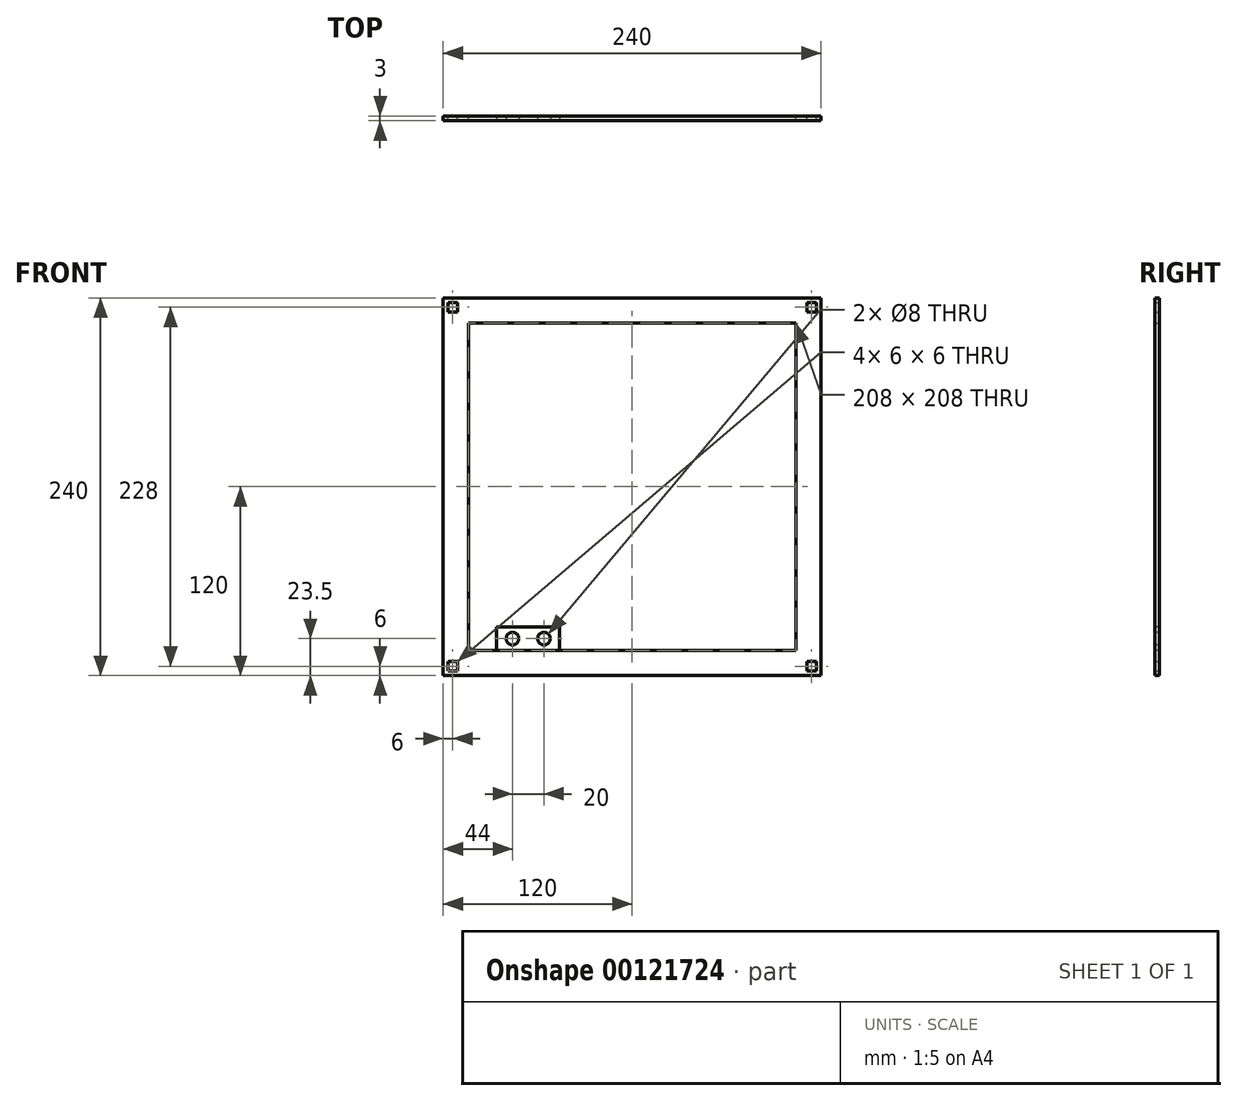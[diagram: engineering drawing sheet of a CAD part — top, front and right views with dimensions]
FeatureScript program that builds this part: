
annotation { "Feature Type Name" : "Feature", "Feature Type Description" : "" }
export const myFeature = defineFeature(function(context is Context, id is Id, definition is map)
    precondition{}
    {
        {
            assignVariable(context, id + "F0", {"name" : "thicknessWood", "anyValue" : 3});
        }
        {
            var Q0;
            Q0=qCreatedBy(makeId("Front.planeOp"),FACE);
            var sketch = newSketch(context, id + "F1", { "sketchPlane" : qUnion([Q0])});
            skLineSegment(sketch, "E0.bottom", {"start": v(0, 0) * mm, "end": v(240, 0) * mm});
            skLineSegment(sketch, "E0.top", {"start": v(0, 240) * mm, "end": v(240, 240) * mm});
            skLineSegment(sketch, "E0.left", {"start": v(0, 0) * mm, "end": v(0, 240) * mm});
            skLineSegment(sketch, "E0.right", {"start": v(240, 0) * mm, "end": v(240, 240) * mm});
            skLineSegment(sketch, "E1.bottom", {"start": v(16, 224) * mm, "end": v(224, 224) * mm});
            skLineSegment(sketch, "E1.top", {"start": v(16, 16) * mm, "end": v(224, 16) * mm});
            skLineSegment(sketch, "E1.left", {"start": v(16, 224) * mm, "end": v(16, 16) * mm});
            skLineSegment(sketch, "E1.right", {"start": v(224, 224) * mm, "end": v(224, 16) * mm});
            skLineSegment(sketch, "E2.bottom", {"start": v(9, 237) * mm, "end": v(3, 237) * mm});
            skLineSegment(sketch, "E2.top", {"start": v(9, 231) * mm, "end": v(3, 231) * mm});
            skLineSegment(sketch, "E2.left", {"start": v(9, 237) * mm, "end": v(9, 231) * mm});
            skLineSegment(sketch, "E2.right", {"start": v(3, 237) * mm, "end": v(3, 231) * mm});
            skLineSegment(sketch, "E3", {"start": v(120, 240) * mm, "end": v(120, 0) * mm, "construction": true});
            skLineSegment(sketch, "E4", {"start": v(0, 120) * mm, "end": v(240, 120) * mm, "construction": true});
            skSolve(sketch);
        }
        {
            var Q0;
            Q0=makeQuery(id+"F1.imprint","IMPRINT",FACE,{"disambiguationData":[TD([[makeQuery(id+"F1.imprint","IMPRINT",EDGE,{"derivedFrom":sQuery(id+"F1.wireOp",EDGE,"E0.bottom")}),1.0]])]});
            var Q1;
            Q1=makeQuery(id+"F1.imprint","IMPRINT",FACE,{"disambiguationData":[TD([[makeQuery(id+"F1.imprint","IMPRINT",EDGE,{"derivedFrom":sQuery(id+"F1.wireOp",EDGE,"E2.bottom")}),1.0]])]});
            var Q2;
            Q2=sQuery(id+"F1.wireOp",EDGE,"E1.left");
            extrude(context, id + "F2", {"entities" : qUnion([Q0, Q1]), "surfaceEntities" : qUnion([Q2]), "depth" : (getVariable(context, 'thicknessWood')) * mm});
        }
        {
            var Q0;
            Q0=makeQuery(id+"F1.imprint","IMPRINT",FACE,{"disambiguationData":[TD([[makeQuery(id+"F1.imprint","IMPRINT",EDGE,{"derivedFrom":sQuery(id+"F1.wireOp",EDGE,"E2.bottom")}),1.0]])]});
            extrude(context, id + "F3", {"entities" : qUnion([Q0]), "operationType" : NewBodyOperationType.REMOVE, "depth" : 25 * mm});
        }
        {
            var Q0;
            Q0=makeQuery(id+"F2.opExtrude","SWEPT_FACE",FACE,{"disambiguationData":[OSD([sQuery(id+"F1.wireOp",EDGE,"E0.left")])]});
            var Q1;
            Q1=makeQuery(id+"F2.opExtrude","SWEPT_FACE",FACE,{"disambiguationData":[OSD([sQuery(id+"F1.wireOp",EDGE,"E0.right")])]});
            cPlane(context, id + "F4", {"entities" : qUnion([Q0, Q1]), "cplaneType" : CPlaneType.MID_PLANE, "offset" : 25 * mm, "width" : 150 * mm, "height" : 150 * mm});
        }
        {
            var Q0;
            Q0=makeQuery(id+"F2.opExtrude","SWEPT_BODY",BODY,{"disambiguationData":[OSD([sQuery(id+"F1.wireOp",EDGE,"E0.bottom"),sQuery(id+"F1.wireOp",EDGE,"E0.top"),sQuery(id+"F1.wireOp",EDGE,"E0.left"),sQuery(id+"F1.wireOp",EDGE,"E0.right"),sQuery(id+"F1.wireOp",EDGE,"E1.bottom"),sQuery(id+"F1.wireOp",EDGE,"E1.top"),sQuery(id+"F1.wireOp",EDGE,"E1.left"),sQuery(id+"F1.wireOp",EDGE,"E1.right")])]});
            var Q1;
            Q1=qCreatedBy(id+"F4.planeOp",FACE);
            mirror(context, id + "F5", {"operationType" : NewBodyOperationType.INTERSECT, "entities" : qUnion([Q0]), "mirrorPlane" : qUnion([Q1])});
        }
        {
            var Q0;
            Q0=makeQuery(id+"F2.opExtrude","SWEPT_FACE",FACE,{"disambiguationData":[OSD([sQuery(id+"F1.wireOp",EDGE,"E0.top")])]});
            var Q1;
            Q1=makeQuery(id+"F2.opExtrude","SWEPT_FACE",FACE,{"disambiguationData":[OSD([sQuery(id+"F1.wireOp",EDGE,"E0.bottom")])]});
            cPlane(context, id + "F6", {"entities" : qUnion([Q0, Q1]), "cplaneType" : CPlaneType.MID_PLANE, "offset" : 25 * mm, "width" : 150 * mm, "height" : 150 * mm});
        }
        {
            var Q0;
            Q0=makeQuery(id+"F2.opExtrude","SWEPT_BODY",BODY,{"disambiguationData":[OSD([sQuery(id+"F1.wireOp",EDGE,"E0.bottom"),sQuery(id+"F1.wireOp",EDGE,"E0.top"),sQuery(id+"F1.wireOp",EDGE,"E0.left"),sQuery(id+"F1.wireOp",EDGE,"E0.right"),sQuery(id+"F1.wireOp",EDGE,"E1.bottom"),sQuery(id+"F1.wireOp",EDGE,"E1.top"),sQuery(id+"F1.wireOp",EDGE,"E1.left"),sQuery(id+"F1.wireOp",EDGE,"E1.right")])]});
            var Q1;
            Q1=qCreatedBy(id+"F6.planeOp",FACE);
            mirror(context, id + "F7", {"operationType" : NewBodyOperationType.INTERSECT, "entities" : qUnion([Q0]), "mirrorPlane" : qUnion([Q1])});
        }
        {
            var Q0;
            Q0=makeQuery(id+"F2.opExtrude","CAP_FACE",FACE,{"disambiguationData":[OSD([sQuery(id+"F1.wireOp",EDGE,"E0.bottom"),sQuery(id+"F1.wireOp",EDGE,"E0.top"),sQuery(id+"F1.wireOp",EDGE,"E0.left"),sQuery(id+"F1.wireOp",EDGE,"E0.right"),sQuery(id+"F1.wireOp",EDGE,"E1.bottom"),sQuery(id+"F1.wireOp",EDGE,"E1.top"),sQuery(id+"F1.wireOp",EDGE,"E1.left"),sQuery(id+"F1.wireOp",EDGE,"E1.right")])],"isStart":false});
            var sketch = newSketch(context, id + "F8", { "sketchPlane" : qUnion([Q0])});
            skLineSegment(sketch, "E5.bottom", {"start": v(34, 16) * mm, "end": v(74, 16) * mm});
            skLineSegment(sketch, "E5.top", {"start": v(34, 31) * mm, "end": v(74, 31) * mm});
            skLineSegment(sketch, "E5.left", {"start": v(34, 16) * mm, "end": v(34, 31) * mm});
            skLineSegment(sketch, "E5.right", {"start": v(74, 16) * mm, "end": v(74, 31) * mm});
            skCircle(sketch, "E6", {"center": v(44, 23.5) * mm, "radius": 4 * mm});
            skPoint(sketch, "E6.centerSnap0", {"position": v(34, 23.5) * mm});
            skCircle(sketch, "E7", {"center": v(64, 23.5) * mm, "radius": 4 * mm});
            skSolve(sketch);
        }
        {
            var Q0;
            Q0=makeQuery(id+"F8.imprint","IMPRINT",FACE,{"disambiguationData":[TD([[makeQuery(id+"F8.imprint","IMPRINT",EDGE,{"derivedFrom":sQuery(id+"F8.wireOp",EDGE,"E5.bottom")}),1.0]])]});
            extrude(context, id + "F9", {"entities" : qUnion([Q0]), "oppositeDirection" : true, "depth" : (getVariable(context, 'thicknessWood')) * mm});
        }
    });
